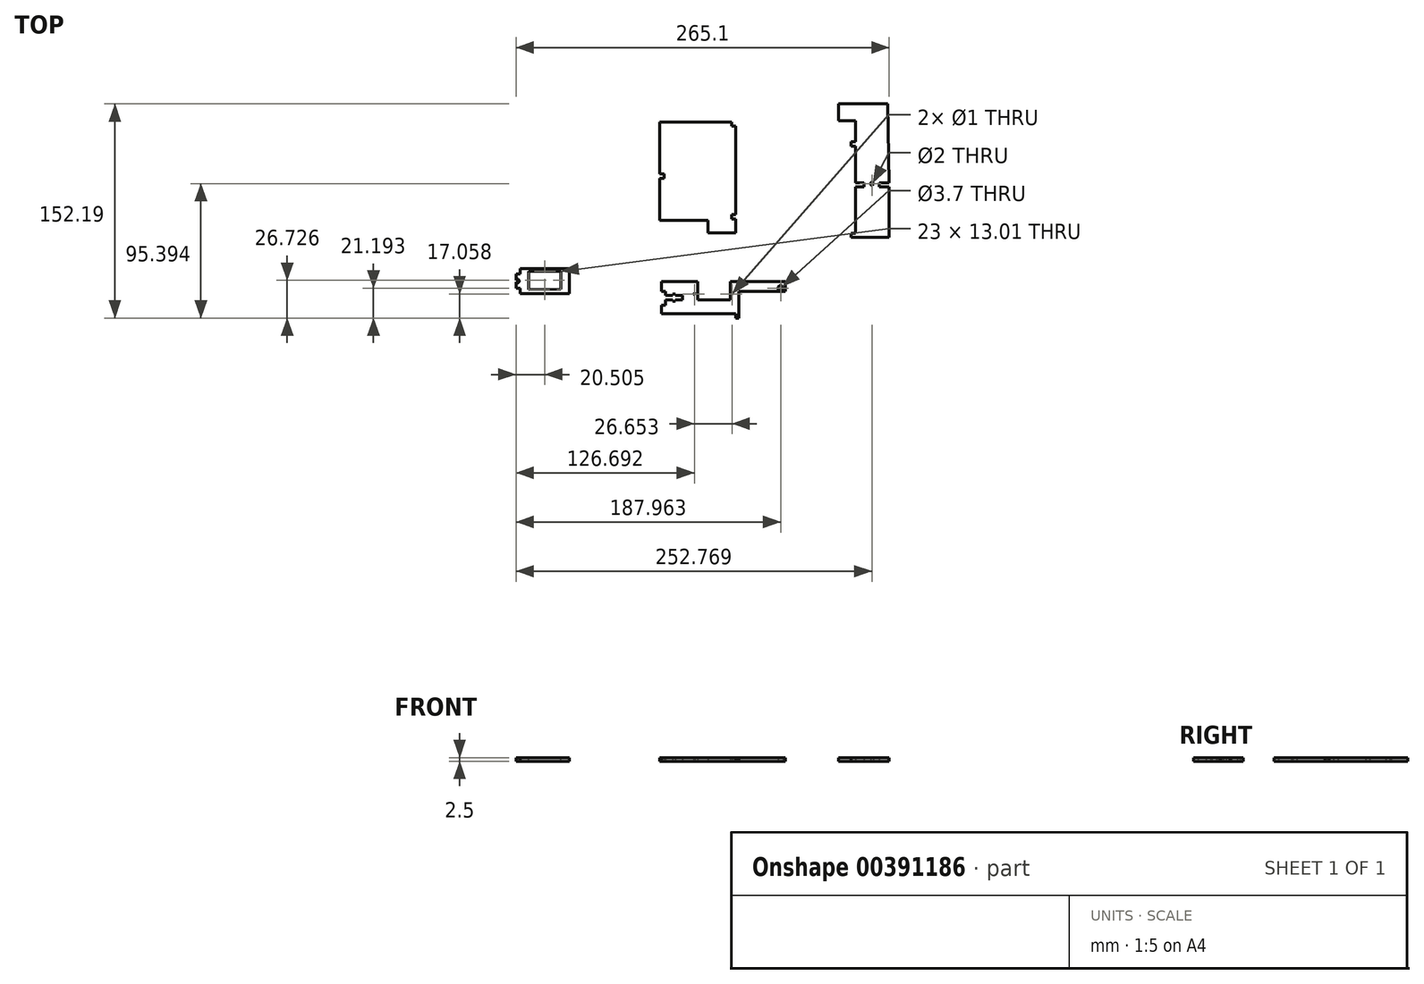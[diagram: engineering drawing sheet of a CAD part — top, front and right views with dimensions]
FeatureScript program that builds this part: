
annotation { "Feature Type Name" : "Feature", "Feature Type Description" : "" }
export const myFeature = defineFeature(function(context is Context, id is Id, definition is map)
    precondition{}
    {
        {
            var Q0;
            Q0=qCreatedBy(makeId("Top.planeOp"),FACE);
            var sketch = newSketch(context, id + "F0", { "sketchPlane" : qUnion([Q0])});
            skLineSegment(sketch, "E0", {"start": v(-54, -55.8) * mm, "end": v(-54, -25.8) * mm});
            skLineSegment(sketch, "E1", {"start": v(-54, -25.8) * mm, "end": v(-51, -25.8) * mm});
            skLineSegment(sketch, "E2", {"start": v(-51, -25.8) * mm, "end": v(-51, -22.8) * mm});
            skLineSegment(sketch, "E3", {"start": v(-51, -22.8) * mm, "end": v(-54, -22.8) * mm});
            skLineSegment(sketch, "E4", {"start": v(-54, -22.8) * mm, "end": v(-54, 14.2) * mm});
            skLineSegment(sketch, "E5", {"start": v(-54, 14.2) * mm, "end": v(-3, 14.2) * mm});
            skLineSegment(sketch, "E6", {"start": v(-3, 14.2) * mm, "end": v(-3, 11.2) * mm});
            skLineSegment(sketch, "E7", {"start": v(-3, 11.2) * mm, "end": v(0, 11.2) * mm});
            skLineSegment(sketch, "E8", {"start": v(0, 11.2) * mm, "end": v(0, -51.8) * mm});
            skLineSegment(sketch, "E9", {"start": v(0, -51.8) * mm, "end": v(-3, -51.8) * mm});
            skLineSegment(sketch, "E10", {"start": v(-3, -51.8) * mm, "end": v(-3, -54.8) * mm});
            skLineSegment(sketch, "E11", {"start": v(-3, -54.8) * mm, "end": v(0, -54.8) * mm});
            skLineSegment(sketch, "E12", {"start": v(0, -54.8) * mm, "end": v(0, -64.8) * mm});
            skLineSegment(sketch, "E13", {"start": v(0, -64.8) * mm, "end": v(-20, -64.8) * mm});
            skLineSegment(sketch, "E14", {"start": v(-54, -55.8) * mm, "end": v(-20, -55.8) * mm});
            skLineSegment(sketch, "E15", {"start": v(-20, -55.8) * mm, "end": v(-20, -64.8) * mm});
            skSolve(sketch);
        }
        {
            var Q0;
            Q0=makeQuery(id+"F0.imprint","IMPRINT",FACE,{"disambiguationData":[TD([[makeQuery(id+"F0.imprint","IMPRINT",EDGE,{"derivedFrom":sQuery(id+"F0.wireOp",EDGE,"E0")}),-1.0]])]});
            extrude(context, id + "F1", {"entities" : qUnion([Q0]), "depth" : 2.5 * mm});
        }
        {
            var Q0;
            Q0=qCreatedBy(makeId("Top.planeOp"),FACE);
            var sketch = newSketch(context, id + "F2", { "sketchPlane" : qUnion([Q0])});
            skLineSegment(sketch, "E16", {"start": v(107.9, 27) * mm, "end": v(72.9, 27) * mm});
            skLineSegment(sketch, "E17", {"start": v(72.9, 27) * mm, "end": v(72.9, 15) * mm});
            skLineSegment(sketch, "E18", {"start": v(72.9, 15) * mm, "end": v(84.9, 15) * mm});
            skLineSegment(sketch, "E19", {"start": v(84.9, 15) * mm, "end": v(84.9, 0) * mm});
            skLineSegment(sketch, "E20", {"start": v(84.9, 0) * mm, "end": v(81.9, 0) * mm});
            skLineSegment(sketch, "E21", {"start": v(81.9, 0) * mm, "end": v(81.9, -3) * mm});
            skLineSegment(sketch, "E22", {"start": v(81.9, -3) * mm, "end": v(84.9, -3) * mm});
            skLineSegment(sketch, "E23", {"start": v(84.9, -3) * mm, "end": v(84.9, -29) * mm});
            skLineSegment(sketch, "E24", {"start": v(84.9, -29) * mm, "end": v(90.9, -29) * mm});
            skLineSegment(sketch, "E25", {"start": v(90.9, -29) * mm, "end": v(90.9, -32) * mm});
            skLineSegment(sketch, "E26", {"start": v(90.9, -32) * mm, "end": v(84.9, -32) * mm});
            skLineSegment(sketch, "E27", {"start": v(84.9, -32) * mm, "end": v(84.9, -65) * mm});
            skLineSegment(sketch, "E28", {"start": v(84.9, -65) * mm, "end": v(81.9, -65) * mm});
            skLineSegment(sketch, "E29", {"start": v(81.9, -65) * mm, "end": v(81.9, -68) * mm});
            skLineSegment(sketch, "E30", {"start": v(81.9, -68) * mm, "end": v(108.9, -68) * mm});
            skLineSegment(sketch, "E31", {"start": v(108.9, -68) * mm, "end": v(108.9, -32) * mm});
            skLineSegment(sketch, "E32", {"start": v(108.9, -32) * mm, "end": v(101.9, -32) * mm});
            skLineSegment(sketch, "E33", {"start": v(101.9, -32) * mm, "end": v(101.9, -29) * mm});
            skLineSegment(sketch, "E34", {"start": v(101.9, -29) * mm, "end": v(108.9, -29) * mm});
            skLineSegment(sketch, "E35", {"start": v(108.9, -29) * mm, "end": v(107.9, 27) * mm});
            skSolve(sketch);
        }
        {
            var Q0;
            Q0=makeQuery(id+"F2.imprint","IMPRINT",FACE,{"disambiguationData":[TD([[makeQuery(id+"F2.imprint","IMPRINT",EDGE,{"derivedFrom":sQuery(id+"F2.wireOp",EDGE,"E16")}),1.0]])]});
            extrude(context, id + "F3", {"entities" : qUnion([Q0]), "depth" : 2.5 * mm});
        }
        {
            var Q0;
            Q0=qCreatedBy(makeId("Top.planeOp"),FACE);
            var sketch = newSketch(context, id + "F4", { "sketchPlane" : qUnion([Q0])});
            skCircle(sketch, "E36", {"center": v(96.57, -29.8) * mm, "radius": 1.5 * mm});
            skSolve(sketch);
        }
        {
            var Q0;
            Q0=sQuery(id+"F4.wireOp",VERTEX,"E36.center");
            var Q1;
            Q1=makeQuery(id+"F3.opExtrude","SWEPT_BODY",BODY,{"disambiguationData":[OSD([sQuery(id+"F2.wireOp",EDGE,"E16"),sQuery(id+"F2.wireOp",EDGE,"E17"),sQuery(id+"F2.wireOp",EDGE,"E18"),sQuery(id+"F2.wireOp",EDGE,"E19"),sQuery(id+"F2.wireOp",EDGE,"E20"),sQuery(id+"F2.wireOp",EDGE,"E21"),sQuery(id+"F2.wireOp",EDGE,"E22"),sQuery(id+"F2.wireOp",EDGE,"E23"),sQuery(id+"F2.wireOp",EDGE,"E24"),sQuery(id+"F2.wireOp",EDGE,"E25"),sQuery(id+"F2.wireOp",EDGE,"E26"),sQuery(id+"F2.wireOp",EDGE,"E27"),sQuery(id+"F2.wireOp",EDGE,"E28"),sQuery(id+"F2.wireOp",EDGE,"E29"),sQuery(id+"F2.wireOp",EDGE,"E30"),sQuery(id+"F2.wireOp",EDGE,"E31"),sQuery(id+"F2.wireOp",EDGE,"E32"),sQuery(id+"F2.wireOp",EDGE,"E33"),sQuery(id+"F2.wireOp",EDGE,"E34"),sQuery(id+"F2.wireOp",EDGE,"E35")])]});
            hole(context, id + "F5", {"style" : HoleStyle.C_SINK, "endStyle" : HoleEndStyle.THROUGH, "oppositeDirection" : true, "holeDiameter" : 2 * mm, "cSinkDiameter" : 3 * mm, "cSinkAngle" : 90 * degree, "isTappedThrough" : true, "tappedDepth" : 12 * mm, "tapClearance" : 3, "locations" : qUnion([Q0]), "scope" : qUnion([Q1])});
        }
        {
            var Q0;
            Q0=qCreatedBy(makeId("Top.planeOp"),FACE);
            var sketch = newSketch(context, id + "F6", { "sketchPlane" : qUnion([Q0])});
            skLineSegment(sketch, "E37", {"start": v(-153.2, -89.96) * mm, "end": v(-118.2, -89.96) * mm});
            skLineSegment(sketch, "E38", {"start": v(-118.2, -89.96) * mm, "end": v(-118.2, -107.96) * mm});
            skLineSegment(sketch, "E39", {"start": v(-118.2, -107.96) * mm, "end": v(-153.2, -107.96) * mm});
            skLineSegment(sketch, "E40", {"start": v(-153.2, -107.96) * mm, "end": v(-153.2, -103.96) * mm});
            skLineSegment(sketch, "E41", {"start": v(-153.2, -103.96) * mm, "end": v(-156.2, -103.96) * mm});
            skLineSegment(sketch, "E42", {"start": v(-156.2, -103.96) * mm, "end": v(-156.2, -93.96) * mm});
            skLineSegment(sketch, "E43", {"start": v(-156.2, -93.96) * mm, "end": v(-153.2, -93.96) * mm});
            skLineSegment(sketch, "E44", {"start": v(-153.2, -93.96) * mm, "end": v(-153.2, -89.96) * mm});
            skSolve(sketch);
        }
        {
            var Q0;
            Q0=makeQuery(id+"F6.imprint","IMPRINT",FACE,{"disambiguationData":[TD([[makeQuery(id+"F6.imprint","IMPRINT",EDGE,{"derivedFrom":sQuery(id+"F6.wireOp",EDGE,"E37")}),-1.0]])]});
            extrude(context, id + "F7", {"entities" : qUnion([Q0]), "depth" : 2.5 * mm});
        }
        {
            var Q0;
            Q0=makeQuery(id+"F7.opExtrude","CAP_FACE",FACE,{"disambiguationData":[OSD([sQuery(id+"F6.wireOp",EDGE,"E37"),sQuery(id+"F6.wireOp",EDGE,"E38"),sQuery(id+"F6.wireOp",EDGE,"E39"),sQuery(id+"F6.wireOp",EDGE,"E40"),sQuery(id+"F6.wireOp",EDGE,"E41"),sQuery(id+"F6.wireOp",EDGE,"E42"),sQuery(id+"F6.wireOp",EDGE,"E43"),sQuery(id+"F6.wireOp",EDGE,"E44")])],"isStart":false});
            var sketch = newSketch(context, id + "F8", { "sketchPlane" : qUnion([Q0])});
            skCircle(sketch, "E45", {"center": v(-155.4, -98.96) * mm, "radius": 1.25 * mm});
            skPoint(sketch, "E45.centerSnap0", {"position": v(-156.2, -98.96) * mm});
            skSolve(sketch);
        }
        {
            var Q0;
            Q0=sQuery(id+"F8.wireOp",VERTEX,"E45.center");
            var Q1;
            Q1=makeQuery(id+"F7.opExtrude","SWEPT_BODY",BODY,{"disambiguationData":[OSD([sQuery(id+"F6.wireOp",EDGE,"E37"),sQuery(id+"F6.wireOp",EDGE,"E38"),sQuery(id+"F6.wireOp",EDGE,"E39"),sQuery(id+"F6.wireOp",EDGE,"E40"),sQuery(id+"F6.wireOp",EDGE,"E41"),sQuery(id+"F6.wireOp",EDGE,"E42"),sQuery(id+"F6.wireOp",EDGE,"E43"),sQuery(id+"F6.wireOp",EDGE,"E44")])]});
            hole(context, id + "F9", {"style" : HoleStyle.C_SINK, "endStyle" : HoleEndStyle.THROUGH, "holeDiameter" : 2 * mm, "cSinkDiameter" : 3 * mm, "cSinkAngle" : 90 * degree, "isTappedThrough" : true, "tappedDepth" : 12 * mm, "tapClearance" : 3, "locations" : qUnion([Q0]), "scope" : qUnion([Q1])});
        }
        {
            var Q0;
            Q0=makeQuery(id+"F7.opExtrude","CAP_FACE",FACE,{"disambiguationData":[OSD([sQuery(id+"F6.wireOp",EDGE,"E37"),sQuery(id+"F6.wireOp",EDGE,"E38"),sQuery(id+"F6.wireOp",EDGE,"E39"),sQuery(id+"F6.wireOp",EDGE,"E40"),sQuery(id+"F6.wireOp",EDGE,"E41"),sQuery(id+"F6.wireOp",EDGE,"E42"),sQuery(id+"F6.wireOp",EDGE,"E43"),sQuery(id+"F6.wireOp",EDGE,"E44")])],"isStart":false});
            var sketch = newSketch(context, id + "F10", { "sketchPlane" : qUnion([Q0])});
            skLineSegment(sketch, "E46", {"start": v(-124.2, -93) * mm, "end": v(-124.2, -104.77) * mm});
            skLineSegment(sketch, "E47", {"start": v(-124.2, -104.77) * mm, "end": v(-147.2, -104.97) * mm});
            skLineSegment(sketch, "E48", {"start": v(-147.2, -104.97) * mm, "end": v(-147.2, -91.96) * mm});
            skLineSegment(sketch, "E49", {"start": v(-147.2, -91.96) * mm, "end": v(-124.2, -91.96) * mm});
            skLineSegment(sketch, "E50", {"start": v(-124.2, -91.96) * mm, "end": v(-124.2, -104.77) * mm});
            skSolve(sketch);
        }
        {
            var Q0;
            {var subQ3=sQuery(id+"F10.wireOp",EDGE,"E47");Q0=makeQuery(id+"F10.imprint","IMPRINT",FACE,{"disambiguationData":[TD([[makeQuery(id+"F10.imprint","IMPRINT",EDGE,{"derivedFrom":subQ3}),-1.0]])]});}
            extrude(context, id + "F11", {"entities" : qUnion([Q0]), "operationType" : NewBodyOperationType.REMOVE, "oppositeDirection" : true, "depth" : 2.5 * mm});
        }
        {
            var Q0;
            Q0=qCreatedBy(makeId("Top.planeOp"),FACE);
            var sketch = newSketch(context, id + "F12", { "sketchPlane" : qUnion([Q0])});
            skLineSegment(sketch, "E51", {"start": v(-53, -99.2) * mm, "end": v(-27, -99.2) * mm});
            skLineSegment(sketch, "E52", {"start": v(-27, -99.2) * mm, "end": v(-27, -112.2) * mm});
            skLineSegment(sketch, "E53", {"start": v(-27, -112.2) * mm, "end": v(-4, -112.2) * mm});
            skLineSegment(sketch, "E54", {"start": v(-4, -112.2) * mm, "end": v(-4, -99.2) * mm});
            skLineSegment(sketch, "E55", {"start": v(-4, -99.2) * mm, "end": v(35, -99.2) * mm});
            skLineSegment(sketch, "E56", {"start": v(35, -99.2) * mm, "end": v(35, -106.2) * mm});
            skLineSegment(sketch, "E57", {"start": v(35, -106.2) * mm, "end": v(2, -106.2) * mm});
            skLineSegment(sketch, "E58", {"start": v(2, -106.2) * mm, "end": v(2, -125.2) * mm});
            skLineSegment(sketch, "E59", {"start": v(2, -125.2) * mm, "end": v(0, -125.2) * mm});
            skLineSegment(sketch, "E60", {"start": v(0, -125.2) * mm, "end": v(0, -122.2) * mm});
            skLineSegment(sketch, "E61", {"start": v(0, -122.2) * mm, "end": v(-53, -122.2) * mm});
            skLineSegment(sketch, "E62", {"start": v(-53, -122.2) * mm, "end": v(-53, -116.2) * mm});
            skLineSegment(sketch, "E63", {"start": v(-53, -116.2) * mm, "end": v(-50, -116.2) * mm});
            skLineSegment(sketch, "E64", {"start": v(-50, -116.2) * mm, "end": v(-50, -112.2) * mm});
            skLineSegment(sketch, "E65", {"start": v(-50, -112.2) * mm, "end": v(-45, -112.2) * mm});
            skLineSegment(sketch, "E66", {"start": v(-45, -112.2) * mm, "end": v(-45, -113.2) * mm});
            skLineSegment(sketch, "E67", {"start": v(-45, -113.2) * mm, "end": v(-43, -113.2) * mm});
            skLineSegment(sketch, "E68", {"start": v(-43, -113.2) * mm, "end": v(-43, -112.2) * mm});
            skLineSegment(sketch, "E69", {"start": v(-43, -112.2) * mm, "end": v(-38, -112.2) * mm});
            skLineSegment(sketch, "E70", {"start": v(-38, -112.2) * mm, "end": v(-38, -109.2) * mm});
            skLineSegment(sketch, "E71", {"start": v(-38, -109.2) * mm, "end": v(-43, -109.2) * mm});
            skLineSegment(sketch, "E72", {"start": v(-43, -109.2) * mm, "end": v(-43, -108.2) * mm});
            skLineSegment(sketch, "E73", {"start": v(-43, -108.2) * mm, "end": v(-45, -108.2) * mm});
            skLineSegment(sketch, "E74", {"start": v(-45, -108.2) * mm, "end": v(-45, -109.2) * mm});
            skLineSegment(sketch, "E75", {"start": v(-45, -109.2) * mm, "end": v(-50.02, -109.2) * mm});
            skLineSegment(sketch, "E76", {"start": v(-50.02, -109.2) * mm, "end": v(-50.02, -106.2) * mm});
            skLineSegment(sketch, "E77", {"start": v(-50.02, -106.2) * mm, "end": v(-52.96, -106.2) * mm});
            skLineSegment(sketch, "E78", {"start": v(-52.96, -106.2) * mm, "end": v(-53, -99.2) * mm});
            skCircle(sketch, "E79", {"center": v(31.76, -104) * mm, "radius": 1.85 * mm});
            skCircle(sketch, "E80", {"center": v(-2.86, -108.13) * mm, "radius": 0.5 * mm});
            skCircle(sketch, "E81", {"center": v(-29.5, -108.13) * mm, "radius": 0.5 * mm});
            skSolve(sketch);
        }
        {
            var Q0;
            Q0=makeQuery(id+"F12.imprint","IMPRINT",FACE,{"disambiguationData":[TD([[makeQuery(id+"F12.imprint","IMPRINT",EDGE,{"derivedFrom":sQuery(id+"F12.wireOp",EDGE,"E51")}),-1.0]])]});
            extrude(context, id + "F13", {"entities" : qUnion([Q0]), "depth" : 2.5 * mm});
        }
    });
